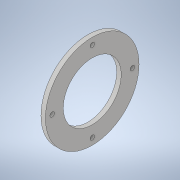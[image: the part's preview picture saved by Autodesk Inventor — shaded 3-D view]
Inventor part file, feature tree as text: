
AUTODESK INVENTOR PART (.ipt)
format: ipt  version: 2021 (Build 250183000, 183)  size: 112,640 bytes
history: native  units: in
note: dims shown in document units (in); Inventor stores cm internally (conversion verified against a paired STEP export)
features: extrude x1, sketch x1
ambient origin geometry x8: Origin, YZ Plane, XZ Plane, XY Plane, X Axis, Y Axis, Z Axis, Center Point
bodies: Body1 (feature_tree)
feature tree (2):
  extrude  "Extrusion3"  Depth=0.25in
  sketch  "Sketch3"  dims[d13=5.25in d14=0.25in d15=1.5748in d17=360.0deg d19=2.25in d20=3.25in d21=0.25in d22=0.0in]
